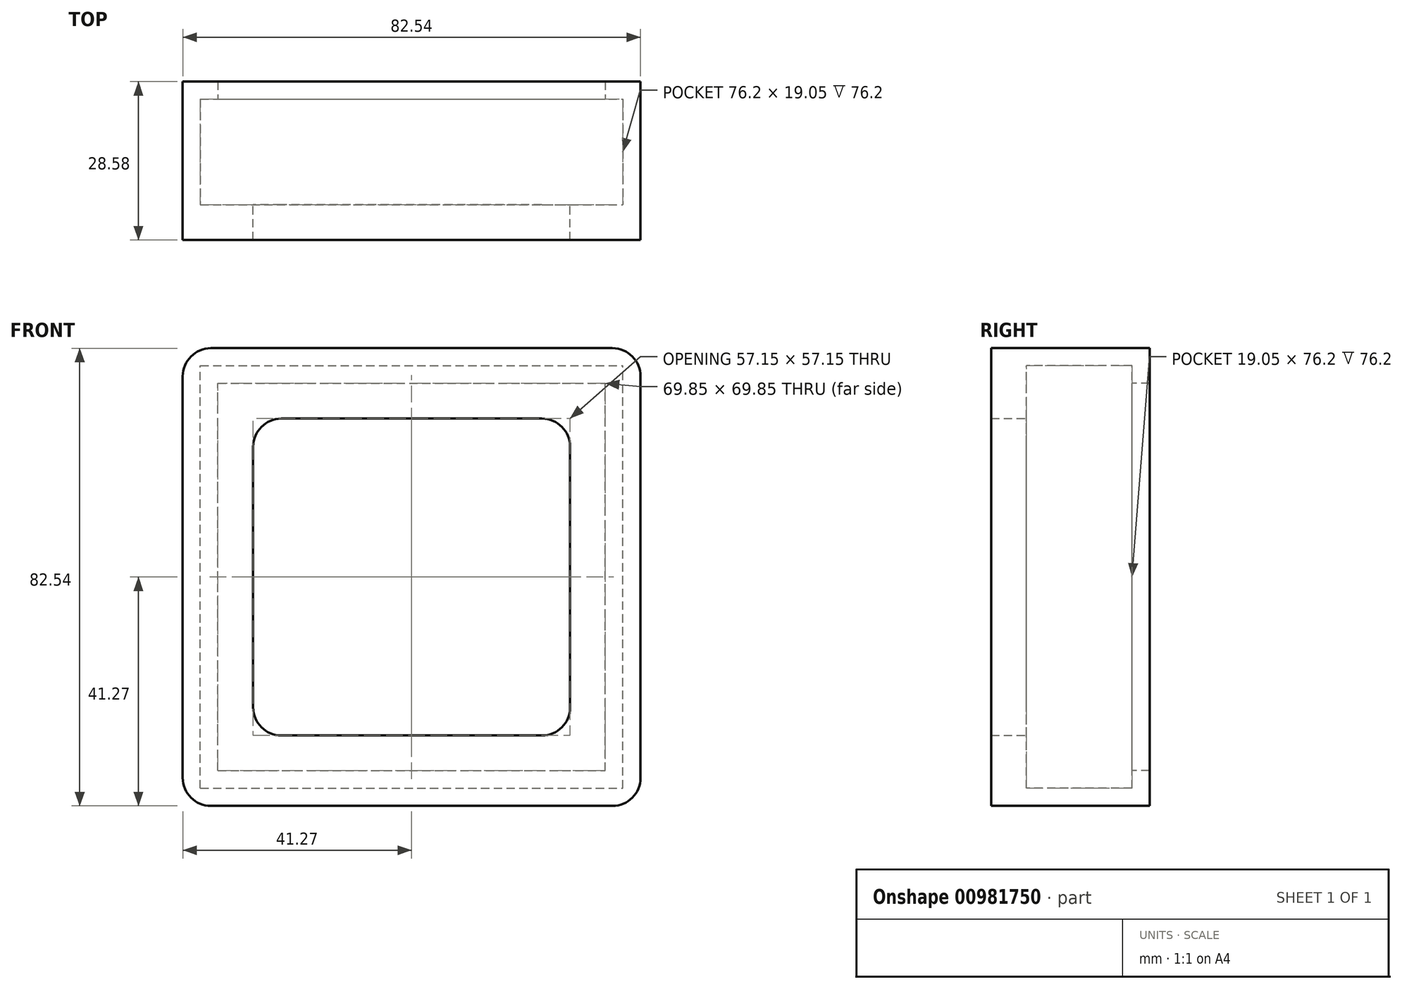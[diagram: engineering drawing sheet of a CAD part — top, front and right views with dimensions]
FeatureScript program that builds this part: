
annotation { "Feature Type Name" : "Feature", "Feature Type Description" : "" }
export const myFeature = defineFeature(function(context is Context, id is Id, definition is map)
    precondition{}
    {
        {
            var Q0;
            Q0=qCreatedBy(makeId("Front.planeOp"),FACE);
            var sketch = newSketch(context, id + "F0", { "sketchPlane" : qUnion([Q0])});
            skLineSegment(sketch, "E0.bottom", {"start": v(41.28, 41.28) * mm, "end": v(-41.28, 41.28) * mm});
            skLineSegment(sketch, "E0.top", {"start": v(41.28, -41.28) * mm, "end": v(-41.28, -41.28) * mm});
            skLineSegment(sketch, "E0.left", {"start": v(41.27, 41.27) * mm, "end": v(41.28, -41.28) * mm});
            skLineSegment(sketch, "E0.right", {"start": v(-41.28, 41.27) * mm, "end": v(-41.27, -41.28) * mm});
            skPoint(sketch, "E0.middle", {"position": v(0, 0) * mm});
            skLineSegment(sketch, "E1.bottom", {"start": v(28.58, -28.58) * mm, "end": v(-28.58, -28.58) * mm});
            skLineSegment(sketch, "E1.top", {"start": v(28.58, 28.57) * mm, "end": v(-28.58, 28.57) * mm});
            skLineSegment(sketch, "E1.left", {"start": v(28.58, -28.58) * mm, "end": v(28.58, 28.57) * mm});
            skLineSegment(sketch, "E1.right", {"start": v(-28.58, -28.58) * mm, "end": v(-28.58, 28.57) * mm});
            skSolve(sketch);
        }
        {
            var Q0;
            Q0=makeQuery(id+"F0.imprint","IMPRINT",FACE,{"disambiguationData":[TD([[makeQuery(id+"F0.imprint","IMPRINT",EDGE,{"derivedFrom":sQuery(id+"F0.wireOp",EDGE,"E0.bottom")}),1.0]])]});
            extrude(context, id + "F1", {"entities" : qUnion([Q0]), "depth" : 6.35 * mm, "offsetDistance" : 25.4 * mm});
        }
        {
            var Q0;
            Q0=makeQuery(id+"F1.opExtrude","CAP_FACE",FACE,{"disambiguationData":[OSD([sQuery(id+"F0.wireOp",EDGE,"E0.bottom"),sQuery(id+"F0.wireOp",EDGE,"E0.top"),sQuery(id+"F0.wireOp",EDGE,"E0.left"),sQuery(id+"F0.wireOp",EDGE,"E0.right"),sQuery(id+"F0.wireOp",EDGE,"E1.bottom"),sQuery(id+"F0.wireOp",EDGE,"E1.top"),sQuery(id+"F0.wireOp",EDGE,"E1.left"),sQuery(id+"F0.wireOp",EDGE,"E1.right")])],"isStart":true});
            var sketch = newSketch(context, id + "F2", { "sketchPlane" : qUnion([Q0])});
            skLineSegment(sketch, "E2.bottom", {"start": v(38.1, -38.1) * mm, "end": v(-38.1, -38.1) * mm});
            skLineSegment(sketch, "E2.top", {"start": v(38.1, 38.1) * mm, "end": v(-38.1, 38.1) * mm});
            skLineSegment(sketch, "E2.left", {"start": v(38.1, -38.1) * mm, "end": v(38.1, 38.1) * mm});
            skLineSegment(sketch, "E2.right", {"start": v(-38.1, -38.1) * mm, "end": v(-38.1, 38.1) * mm});
            skPoint(sketch, "E2.middle", {"position": v(0, 0) * mm});
            skLineSegment(sketch, "E3.bottom", {"start": v(41.27, -41.28) * mm, "end": v(-41.27, -41.28) * mm});
            skLineSegment(sketch, "E3.top", {"start": v(41.27, 41.28) * mm, "end": v(-41.27, 41.28) * mm});
            skLineSegment(sketch, "E3.left", {"start": v(41.27, -41.28) * mm, "end": v(41.27, 41.28) * mm});
            skLineSegment(sketch, "E3.right", {"start": v(-41.27, -41.28) * mm, "end": v(-41.27, 41.28) * mm});
            skSolve(sketch);
        }
        {
            var Q0;
            Q0 = qSketchRegion(id + "F2", true);
            extrude(context, id + "F3", {"entities" : qUnion([Q0]), "operationType" : NewBodyOperationType.ADD, "depth" : 19.05 * mm, "offsetDistance" : 25.4 * mm});
        }
        {
            var Q0;
            Q0=makeQuery(id+"F3.opExtrude","CAP_FACE",FACE,{"disambiguationData":[OSD([sQuery(id+"F2.wireOp",EDGE,"E2.bottom"),sQuery(id+"F2.wireOp",EDGE,"E2.top"),sQuery(id+"F2.wireOp",EDGE,"E2.left"),sQuery(id+"F2.wireOp",EDGE,"E2.right"),sQuery(id+"F2.wireOp",EDGE,"E3.bottom"),sQuery(id+"F2.wireOp",EDGE,"E3.top"),sQuery(id+"F2.wireOp",EDGE,"E3.left"),sQuery(id+"F2.wireOp",EDGE,"E3.right")])],"isStart":false});
            var sketch = newSketch(context, id + "F4", { "sketchPlane" : qUnion([Q0])});
            skLineSegment(sketch, "E4.bottom", {"start": v(41.27, -41.28) * mm, "end": v(-41.27, -41.28) * mm});
            skLineSegment(sketch, "E4.top", {"start": v(41.27, 41.28) * mm, "end": v(-41.27, 41.28) * mm});
            skLineSegment(sketch, "E4.left", {"start": v(41.27, -41.28) * mm, "end": v(41.27, 41.28) * mm});
            skLineSegment(sketch, "E4.right", {"start": v(-41.27, -41.28) * mm, "end": v(-41.27, 41.28) * mm});
            skPoint(sketch, "E4.middle", {"position": v(0, 0) * mm});
            skLineSegment(sketch, "E5.bottom", {"start": v(34.92, -34.93) * mm, "end": v(-34.92, -34.93) * mm});
            skLineSegment(sketch, "E5.top", {"start": v(34.92, 34.93) * mm, "end": v(-34.92, 34.93) * mm});
            skLineSegment(sketch, "E5.left", {"start": v(34.92, -34.93) * mm, "end": v(34.92, 34.93) * mm});
            skLineSegment(sketch, "E5.right", {"start": v(-34.92, -34.93) * mm, "end": v(-34.92, 34.93) * mm});
            skSolve(sketch);
        }
        {
            var Q0;
            Q0 = qSketchRegion(id + "F4", true);
            extrude(context, id + "F5", {"entities" : qUnion([Q0]), "operationType" : NewBodyOperationType.ADD, "depth" : 3.17 * mm, "offsetDistance" : 25.4 * mm});
        }
        {
            var Q0;
            Q0=makeQuery(id+"F5.boolean.opBoolean","MERGE",EDGE,{"derivedFrom":[makeQuery(id+"F3.boolean.opBoolean","MERGE",EDGE,{"derivedFrom":[makeQuery(id+"F1.opExtrude","SWEPT_EDGE",EDGE,{"disambiguationData":[OSD([sQuery(id+"F0.wireOp",EDGE,"E0.top"),sQuery(id+"F0.wireOp",EDGE,"E0.left")])]}),makeQuery(id+"F3.opExtrude","SWEPT_EDGE",EDGE,{"disambiguationData":[OSD([sQuery(id+"F2.wireOp",EDGE,"E3.bottom"),sQuery(id+"F2.wireOp",EDGE,"E3.right")])]})]}),makeQuery(id+"F5.opExtrude","SWEPT_EDGE",EDGE,{"disambiguationData":[OSD([sQuery(id+"F4.wireOp",EDGE,"E4.bottom"),sQuery(id+"F4.wireOp",EDGE,"E4.right")])]})]});
            var Q1;
            Q1=makeQuery(id+"F5.boolean.opBoolean","MERGE",EDGE,{"derivedFrom":[makeQuery(id+"F3.boolean.opBoolean","MERGE",EDGE,{"derivedFrom":[makeQuery(id+"F1.opExtrude","SWEPT_EDGE",EDGE,{"disambiguationData":[OSD([sQuery(id+"F0.wireOp",EDGE,"E0.bottom"),sQuery(id+"F0.wireOp",EDGE,"E0.left")])]}),makeQuery(id+"F3.opExtrude","SWEPT_EDGE",EDGE,{"disambiguationData":[OSD([sQuery(id+"F2.wireOp",EDGE,"E3.top"),sQuery(id+"F2.wireOp",EDGE,"E3.right")])]})]}),makeQuery(id+"F5.opExtrude","SWEPT_EDGE",EDGE,{"disambiguationData":[OSD([sQuery(id+"F4.wireOp",EDGE,"E4.top"),sQuery(id+"F4.wireOp",EDGE,"E4.right")])]})]});
            var Q2;
            Q2=makeQuery(id+"F5.boolean.opBoolean","MERGE",EDGE,{"derivedFrom":[makeQuery(id+"F3.boolean.opBoolean","MERGE",EDGE,{"derivedFrom":[makeQuery(id+"F1.opExtrude","SWEPT_EDGE",EDGE,{"disambiguationData":[OSD([sQuery(id+"F0.wireOp",EDGE,"E0.bottom"),sQuery(id+"F0.wireOp",EDGE,"E0.right")])]}),makeQuery(id+"F3.opExtrude","SWEPT_EDGE",EDGE,{"disambiguationData":[OSD([sQuery(id+"F2.wireOp",EDGE,"E3.top"),sQuery(id+"F2.wireOp",EDGE,"E3.left")])]})]}),makeQuery(id+"F5.opExtrude","SWEPT_EDGE",EDGE,{"disambiguationData":[OSD([sQuery(id+"F4.wireOp",EDGE,"E4.top"),sQuery(id+"F4.wireOp",EDGE,"E4.left")])]})]});
            var Q3;
            Q3=makeQuery(id+"F5.boolean.opBoolean","MERGE",EDGE,{"derivedFrom":[makeQuery(id+"F3.boolean.opBoolean","MERGE",EDGE,{"derivedFrom":[makeQuery(id+"F1.opExtrude","SWEPT_EDGE",EDGE,{"disambiguationData":[OSD([sQuery(id+"F0.wireOp",EDGE,"E0.top"),sQuery(id+"F0.wireOp",EDGE,"E0.right")])]}),makeQuery(id+"F3.opExtrude","SWEPT_EDGE",EDGE,{"disambiguationData":[OSD([sQuery(id+"F2.wireOp",EDGE,"E3.bottom"),sQuery(id+"F2.wireOp",EDGE,"E3.left")])]})]}),makeQuery(id+"F5.opExtrude","SWEPT_EDGE",EDGE,{"disambiguationData":[OSD([sQuery(id+"F4.wireOp",EDGE,"E4.bottom"),sQuery(id+"F4.wireOp",EDGE,"E4.left")])]})]});
            fillet(context, id + "F6", {"entities" : qUnion([Q0, Q1, Q2, Q3]), "radius" : 5.08 * mm, "tangentPropagation" : true, "allowEdgeOverflow" : false});
        }
        {
            var Q0;
            Q0=makeQuery(id+"F1.opExtrude","SWEPT_EDGE",EDGE,{"disambiguationData":[OSD([sQuery(id+"F0.wireOp",EDGE,"E1.bottom"),sQuery(id+"F0.wireOp",EDGE,"E1.right")])]});
            var Q1;
            Q1=makeQuery(id+"F1.opExtrude","SWEPT_EDGE",EDGE,{"disambiguationData":[OSD([sQuery(id+"F0.wireOp",EDGE,"E1.bottom"),sQuery(id+"F0.wireOp",EDGE,"E1.left")])]});
            var Q2;
            Q2=makeQuery(id+"F1.opExtrude","SWEPT_EDGE",EDGE,{"disambiguationData":[OSD([sQuery(id+"F0.wireOp",EDGE,"E1.top"),sQuery(id+"F0.wireOp",EDGE,"E1.left")])]});
            var Q3;
            Q3=makeQuery(id+"F1.opExtrude","SWEPT_EDGE",EDGE,{"disambiguationData":[OSD([sQuery(id+"F0.wireOp",EDGE,"E1.top"),sQuery(id+"F0.wireOp",EDGE,"E1.right")])]});
            fillet(context, id + "F7", {"entities" : qUnion([Q0, Q1, Q2, Q3]), "radius" : 5.08 * mm, "tangentPropagation" : true, "allowEdgeOverflow" : false});
        }
    });
